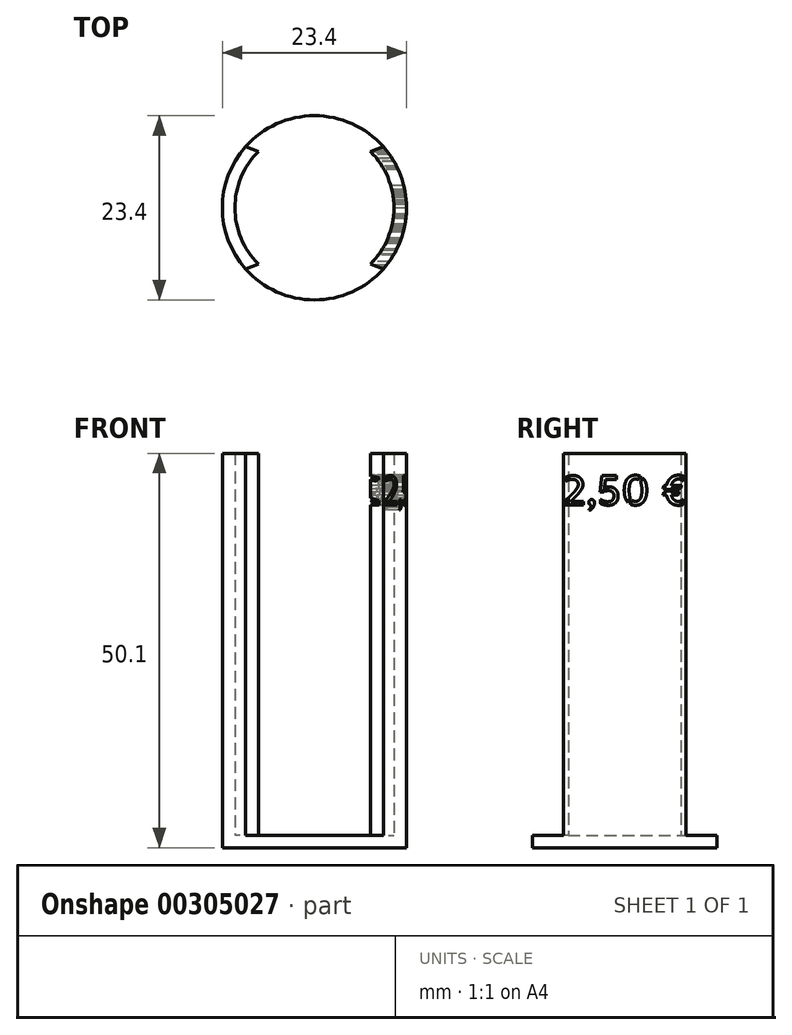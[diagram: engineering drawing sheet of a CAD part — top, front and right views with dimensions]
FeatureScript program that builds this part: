
annotation { "Feature Type Name" : "Feature", "Feature Type Description" : "" }
export const myFeature = defineFeature(function(context is Context, id is Id, definition is map)
    precondition{}
    {
        {
            var Q0;
            Q0=qCreatedBy(makeId("Top.planeOp"),FACE);
            var sketch = newSketch(context, id + "F0", { "sketchPlane" : qUnion([Q0])});
            skCircle(sketch, "E0", {"center": v(0, 0) * mm, "radius": 10.1 * mm});
            skCircle(sketch, "E1.0", {"center": v(0, 0) * mm, "radius": 11.7 * mm});
            skSolve(sketch);
        }
        {
            var Q0;
            Q0=makeQuery(id+"F0.imprint","IMPRINT",FACE,{"disambiguationData":[TD([[makeQuery(id+"F0.imprint","IMPRINT",EDGE,{"derivedFrom":sQuery(id+"F0.wireOp",EDGE,"E0")}),1.0]])]});
            var Q1;
            Q1=makeQuery(id+"F0.imprint","IMPRINT",FACE,{"disambiguationData":[TD([[makeQuery(id+"F0.imprint","IMPRINT",EDGE,{"derivedFrom":sQuery(id+"F0.wireOp",EDGE,"E0")}),-1.0]])]});
            extrude(context, id + "F1", {"entities" : qUnion([Q0, Q1]), "oppositeDirection" : true, "depth" : 1.6 * mm});
        }
        {
            var Q0;
            Q0=makeQuery(id+"F0.imprint","IMPRINT",FACE,{"disambiguationData":[TD([[makeQuery(id+"F0.imprint","IMPRINT",EDGE,{"derivedFrom":sQuery(id+"F0.wireOp",EDGE,"E0")}),-1.0]])]});
            extrude(context, id + "F2", {"entities" : qUnion([Q0]), "operationType" : NewBodyOperationType.ADD, "depth" : 48.5 * mm});
        }
        {
            var Q0;
            Q0=qCreatedBy(makeId("Front.planeOp"),FACE);
            var sketch = newSketch(context, id + "F3", { "sketchPlane" : qUnion([Q0])});
            skLineSegment(sketch, "E2.bottom", {"start": v(-7, 48.5) * mm, "end": v(7, 48.5) * mm});
            skLineSegment(sketch, "E2.top", {"start": v(-7, 0) * mm, "end": v(7, 0) * mm});
            skLineSegment(sketch, "E2.left", {"start": v(-7, 48.5) * mm, "end": v(-7, 0) * mm});
            skLineSegment(sketch, "E2.right", {"start": v(7, 48.5) * mm, "end": v(7, 0) * mm});
            skSolve(sketch);
        }
        {
            var Q0;
            Q0=makeQuery(id+"F3.imprint","IMPRINT",FACE,{"disambiguationData":[TD([[makeQuery(id+"F3.imprint","IMPRINT",EDGE,{"derivedFrom":sQuery(id+"F3.wireOp",EDGE,"E2.bottom")}),-1.0]])]});
            extrude(context, id + "F4", {"entities" : qUnion([Q0]), "operationType" : NewBodyOperationType.REMOVE, "endBound" : BoundingType.THROUGH_ALL, "oppositeDirection" : true, "depth" : 25 * mm, "hasSecondDirection" : true, "secondDirectionBound" : SecondDirectionBoundingType.THROUGH_ALL, "secondDirectionOppositeDirection" : false, "secondDirectionDepth" : 25 * mm});
        }
        {
            var Q0;
            {var subQ0=sQuery(id+"F0.wireOp",EDGE,"E1.0");Q0=makeQuery(id+"F4.boolean.opBoolean","INTERSECT",EDGE,{"disambiguationData":[OD(0.0)],"derivedFrom":[makeQuery(id+"F2.boolean.opBoolean","MERGE",FACE,{"derivedFrom":[makeQuery(id+"F1.opExtrude","SWEPT_FACE",FACE,{"disambiguationData":[OSD([subQ0])]}),makeQuery(id+"F2.opExtrude","SWEPT_FACE",FACE,{"disambiguationData":[OSD([subQ0])]})]}),makeQuery(id+"F4.opExtrude","SWEPT_FACE",FACE,{"disambiguationData":[OSD([sQuery(id+"F3.wireOp",EDGE,"E2.left")])]})]});}
            var Q1;
            {var subQ0=sQuery(id+"F0.wireOp",EDGE,"E1.0");Q1=makeQuery(id+"F4.boolean.opBoolean","INTERSECT",EDGE,{"disambiguationData":[OD(0.0)],"derivedFrom":[makeQuery(id+"F2.boolean.opBoolean","MERGE",FACE,{"derivedFrom":[makeQuery(id+"F1.opExtrude","SWEPT_FACE",FACE,{"disambiguationData":[OSD([subQ0])]}),makeQuery(id+"F2.opExtrude","SWEPT_FACE",FACE,{"disambiguationData":[OSD([subQ0])]})]}),makeQuery(id+"F4.opExtrude","SWEPT_FACE",FACE,{"disambiguationData":[OSD([sQuery(id+"F3.wireOp",EDGE,"E2.right")])]})]});}
            var Q2;
            {var subQ0=sQuery(id+"F0.wireOp",EDGE,"E1.0");Q2=makeQuery(id+"F4.boolean.opBoolean","INTERSECT",EDGE,{"disambiguationData":[OD(1.0)],"derivedFrom":[makeQuery(id+"F2.boolean.opBoolean","MERGE",FACE,{"derivedFrom":[makeQuery(id+"F1.opExtrude","SWEPT_FACE",FACE,{"disambiguationData":[OSD([subQ0])]}),makeQuery(id+"F2.opExtrude","SWEPT_FACE",FACE,{"disambiguationData":[OSD([subQ0])]})]}),makeQuery(id+"F4.opExtrude","SWEPT_FACE",FACE,{"disambiguationData":[OSD([sQuery(id+"F3.wireOp",EDGE,"E2.left")])]})]});}
            var Q3;
            {var subQ0=sQuery(id+"F0.wireOp",EDGE,"E1.0");Q3=makeQuery(id+"F4.boolean.opBoolean","INTERSECT",EDGE,{"disambiguationData":[OD(1.0)],"derivedFrom":[makeQuery(id+"F2.boolean.opBoolean","MERGE",FACE,{"derivedFrom":[makeQuery(id+"F1.opExtrude","SWEPT_FACE",FACE,{"disambiguationData":[OSD([subQ0])]}),makeQuery(id+"F2.opExtrude","SWEPT_FACE",FACE,{"disambiguationData":[OSD([subQ0])]})]}),makeQuery(id+"F4.opExtrude","SWEPT_FACE",FACE,{"disambiguationData":[OSD([sQuery(id+"F3.wireOp",EDGE,"E2.right")])]})]});}
            chamfer(context, id + "F5", {"entities" : qUnion([Q0, Q1, Q2, Q3]), "width" : 1 * mm, "tangentPropagation" : true});
        }
        {
            var Q0;
            Q0=qCreatedBy(makeId("Right.planeOp"),FACE);
            var sketch = newSketch(context, id + "F6", { "sketchPlane" : qUnion([Q0])});
            skText(sketch, "E3", { "text": "2,50 €", "fontName": "AllertaStencil-Regular.ttf"});
            const initialGuessF6  = {"E3": [-0.008, 0.04193, 1, 0, 0.00375]};
            skSetInitialGuess(sketch, initialGuessF6);
            skSolve(sketch);
        }
        {
            var Q0;
            Q0=qSketchRegion(id+"F6",true);
            extrude(context, id + "F7", {"entities" : qUnion([Q0]), "operationType" : NewBodyOperationType.REMOVE, "depth" : 25 * mm});
        }
    });
